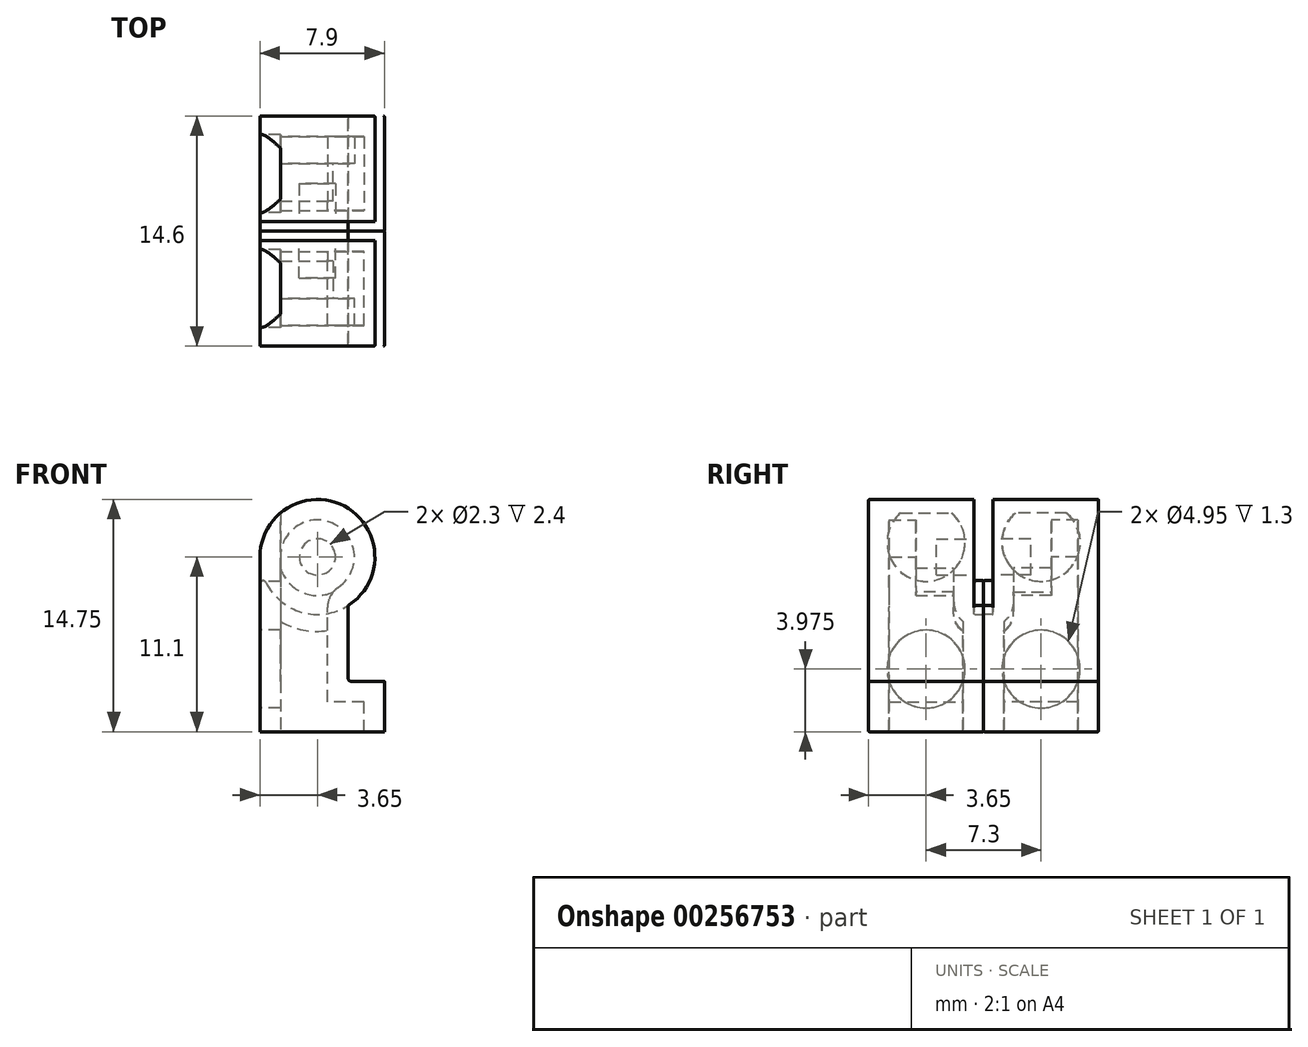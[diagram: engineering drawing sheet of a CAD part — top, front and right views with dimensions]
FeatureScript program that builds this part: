
annotation { "Feature Type Name" : "Feature", "Feature Type Description" : "" }
export const myFeature = defineFeature(function(context is Context, id is Id, definition is map)
    precondition{}
    {
        {
            var Q0;
            Q0=qCreatedBy(makeId("Front.planeOp"),FACE);
            var sketch = newSketch(context, id + "F0", { "sketchPlane" : qUnion([Q0])});
            skArc(sketch, "E0", {"start": v(1.95, -3.09) * mm, "mid": v(1.76, 3.2) * mm, "end": v(-3.65, 0) * mm});
            skLineSegment(sketch, "E1", {"start": v(-3.65, 0) * mm, "end": v(-3.65, -11.1) * mm});
            skLineSegment(sketch, "E2", {"start": v(-3.65, -11.1) * mm, "end": v(4.25, -11.1) * mm});
            skLineSegment(sketch, "E3", {"start": v(4.25, -11.1) * mm, "end": v(4.25, -7.9) * mm});
            skLineSegment(sketch, "E4", {"start": v(4.25, -7.9) * mm, "end": v(1.95, -7.9) * mm});
            skLineSegment(sketch, "E5", {"start": v(1.95, -7.9) * mm, "end": v(1.95, -3.09) * mm});
            skSolve(sketch);
        }
        {
            var Q0;
            Q0=makeQuery(id+"F0.imprint","IMPRINT",FACE,{"disambiguationData":[TD([[makeQuery(id+"F0.imprint","IMPRINT",EDGE,{"derivedFrom":sQuery(id+"F0.wireOp",EDGE,"E0")}),1.0]])]});
            extrude(context, id + "F1", {"entities" : qUnion([Q0]), "depth" : 7.3 * mm});
        }
        {
            var Q0;
            Q0=qCreatedBy(makeId("Front.planeOp"),FACE);
            var sketch = newSketch(context, id + "F2", { "sketchPlane" : qUnion([Q0])});
            skCircle(sketch, "E6", {"center": v(0, 0) * mm, "radius": 3.65 * mm});
            skSolve(sketch);
        }
        {
            var Q0;
            Q0=makeQuery(id+"F2.imprint","IMPRINT",FACE,{"disambiguationData":[TD([[makeQuery(id+"F2.imprint","IMPRINT",EDGE,{"derivedFrom":sQuery(id+"F2.wireOp",EDGE,"E6")}),1.0]])]});
            extrude(context, id + "F3", {"entities" : qUnion([Q0]), "operationType" : NewBodyOperationType.REMOVE, "depth" : 0.6 * mm});
        }
        {
            var Q0;
            Q0=qCreatedBy(makeId("Front.planeOp"),FACE);
            var sketch = newSketch(context, id + "F4", { "sketchPlane" : qUnion([Q0])});
            skCircle(sketch, "E7", {"center": v(0, 0) * mm, "radius": 1.15 * mm});
            skSolve(sketch);
        }
        {
            var Q0;
            Q0=makeQuery(id+"F4.imprint","IMPRINT",FACE,{"disambiguationData":[TD([[makeQuery(id+"F4.imprint","IMPRINT",EDGE,{"derivedFrom":sQuery(id+"F4.wireOp",EDGE,"E7")}),1.0]])]});
            extrude(context, id + "F5", {"entities" : qUnion([Q0]), "operationType" : NewBodyOperationType.REMOVE, "depth" : 3 * mm});
        }
        {
            var Q0;
            {var subQ0=sQuery(id+"F0.wireOp",EDGE,"E5");Q0=makeQuery(id+"F3.boolean.opBoolean","SPLIT",EDGE,{"disambiguationData":[topologyDisambiguationEdgeConnected([makeQuery(id+"F3.opExtrude","SWEPT_FACE",FACE,{"disambiguationData":[OSD([sQuery(id+"F2.wireOp",EDGE,"E6")])]})])],"derivedFrom":makeQuery(id+"F1.opExtrude","SWEPT_EDGE",EDGE,{"disambiguationData":[OSD([sQuery(id+"F0.wireOp",EDGE,"E0"),subQ0])]})});}
            var Q1;
            {var subQ0=sQuery(id+"F0.wireOp",EDGE,"E1");Q1=makeQuery(id+"F3.boolean.opBoolean","SPLIT",EDGE,{"disambiguationData":[topologyDisambiguationEdgeConnected([makeQuery(id+"F3.opExtrude","SWEPT_FACE",FACE,{"disambiguationData":[OSD([sQuery(id+"F2.wireOp",EDGE,"E6")])]})])],"derivedFrom":makeQuery(id+"F1.opExtrude","SWEPT_EDGE",EDGE,{"disambiguationData":[OSD([sQuery(id+"F0.wireOp",EDGE,"E0"),subQ0])]})});}
            fillet(context, id + "F6", {"entities" : qUnion([Q0, Q1]), "radius" : 0.2 * mm, "tangentPropagation" : true, "allowEdgeOverflow" : false});
        }
        {
            var Q0;
            {var subQ0=sQuery(id+"F2.wireOp",EDGE,"E6");Q0=makeQuery(id+"F3.boolean.opBoolean","COPY",EDGE,{"disambiguationData":[topologyDisambiguationEdgeConnected([makeQuery(id+"F3.opExtrude","SWEPT_FACE",FACE,{"disambiguationData":[OSD([subQ0])]})])],"derivedFrom":makeQuery(id+"F3.opExtrude","CAP_EDGE",EDGE,{"disambiguationData":[OSD([subQ0])],"isStart":false})});}
            fillet(context, id + "F7", {"entities" : qUnion([Q0]), "radius" : 0.05 * mm, "tangentPropagation" : true, "allowEdgeOverflow" : false});
        }
        {
            var Q0;
            Q0=makeQuery(id+"F1.opExtrude","SWEPT_FACE",FACE,{"disambiguationData":[OSD([sQuery(id+"F0.wireOp",EDGE,"E2")])]});
            shell(context, id + "F8", {"entities" : qUnion([Q0]), "thickness" : 1.3 * mm});
        }
        {
            var Q0;
            Q0=makeQuery(id+"F1.opExtrude","SWEPT_FACE",FACE,{"disambiguationData":[OSD([sQuery(id+"F0.wireOp",EDGE,"E1")])]});
            var sketch = newSketch(context, id + "F9", { "sketchPlane" : qUnion([Q0])});
            skCircle(sketch, "E8", {"center": v(3.65, -7.12) * mm, "radius": 2.48 * mm});
            skLineSegment(sketch, "E9", {"start": v(3.65, -11.1) * mm, "end": v(3.65, -6.01) * mm, "construction": true});
            skCircle(sketch, "E10", {"center": v(3.65, 0.92) * mm, "radius": 2.48 * mm});
            skSolve(sketch);
        }
        {
            var Q0;
            Q0=qSketchRegion(id+"F9",true);
            var Q1;
            Q1=makeQuery(id+"F8.opShell","OFFSET_FACE",FACE,{"disambiguationData":[OSD([sQuery(id+"F0.wireOp",EDGE,"E1")])]});
            extrude(context, id + "F10", {"entities" : qUnion([Q0]), "operationType" : NewBodyOperationType.REMOVE, "endBound" : BoundingType.UP_TO_SURFACE, "oppositeDirection" : true, "endBoundEntityFace" : qUnion([Q1]), "depth" : 25 * mm});
        }
        {
            var Q0;
            {var subQ0=sQuery(id+"F0.wireOp",EDGE,"E0");var subQ1=sQuery(id+"F0.wireOp",EDGE,"E5");Q0=makeQuery(id+"F3.boolean.opBoolean","SPLIT",EDGE,{"disambiguationData":[topologyDisambiguationEdgeConnected([makeQuery(id+"F1.opExtrude","SWEPT_FACE",FACE,{"disambiguationData":[OSD([subQ0])]})])],"derivedFrom":makeQuery(id+"F1.opExtrude","SWEPT_EDGE",EDGE,{"disambiguationData":[OSD([subQ0,subQ1])]})});}
            var Q1;
            Q1=makeQuery(id+"F1.opExtrude","SWEPT_EDGE",EDGE,{"disambiguationData":[OSD([sQuery(id+"F0.wireOp",EDGE,"E4"),sQuery(id+"F0.wireOp",EDGE,"E5")])]});
            fillet(context, id + "F11", {"entities" : qUnion([Q0, Q1]), "radius" : 0.2 * mm, "tangentPropagation" : true, "allowEdgeOverflow" : false});
        }
        {
            var Q0;
            Q0=makeQuery(id+"F1.opExtrude","CAP_FACE",FACE,{"disambiguationData":[OSD([sQuery(id+"F0.wireOp",EDGE,"E0"),sQuery(id+"F0.wireOp",EDGE,"E1"),sQuery(id+"F0.wireOp",EDGE,"E2"),sQuery(id+"F0.wireOp",EDGE,"E3"),sQuery(id+"F0.wireOp",EDGE,"E4"),sQuery(id+"F0.wireOp",EDGE,"E5")])],"isStart":false});
            var Q1;
            Q1=makeQuery(id+"F1.opExtrude","CAP_FACE",FACE,{"disambiguationData":[OSD([sQuery(id+"F0.wireOp",EDGE,"E0"),sQuery(id+"F0.wireOp",EDGE,"E1"),sQuery(id+"F0.wireOp",EDGE,"E2"),sQuery(id+"F0.wireOp",EDGE,"E3"),sQuery(id+"F0.wireOp",EDGE,"E4"),sQuery(id+"F0.wireOp",EDGE,"E5")])],"isStart":true});
            fillet(context, id + "F12", {"entities" : qUnion([Q0, Q1]), "radius" : 0.05 * mm, "tangentPropagation" : true, "allowEdgeOverflow" : false});
        }
        {
            var Q0;
            Q0=makeQuery(id+"F1.opExtrude","SWEPT_BODY",BODY,{"disambiguationData":[OSD([sQuery(id+"F0.wireOp",EDGE,"E0"),sQuery(id+"F0.wireOp",EDGE,"E1"),sQuery(id+"F0.wireOp",EDGE,"E2"),sQuery(id+"F0.wireOp",EDGE,"E3"),sQuery(id+"F0.wireOp",EDGE,"E4"),sQuery(id+"F0.wireOp",EDGE,"E5")])]});
            var Q1;
            Q1=qCreatedBy(makeId("Front.planeOp"),FACE);
            mirror(context, id + "F13", {"entities" : qUnion([Q0]), "mirrorPlane" : qUnion([Q1])});
        }
    });
